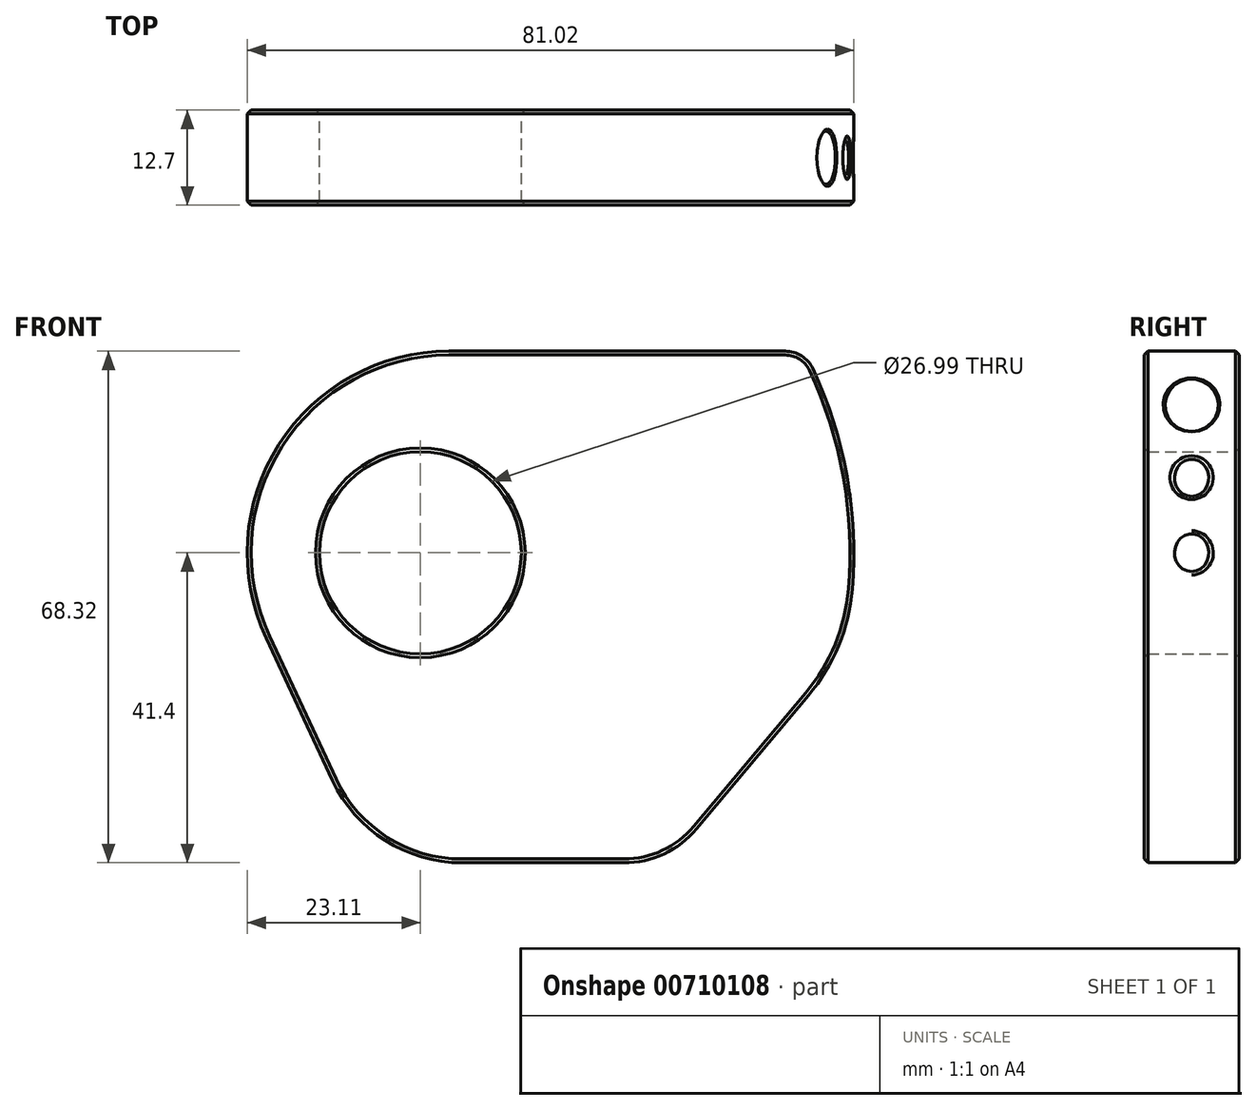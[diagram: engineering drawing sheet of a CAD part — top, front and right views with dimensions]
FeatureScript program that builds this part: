
annotation { "Feature Type Name" : "Feature", "Feature Type Description" : "" }
export const myFeature = defineFeature(function(context is Context, id is Id, definition is map)
    precondition{}
    {
        {
            assignVariable(context, id + "F0", {"name" : "DetentDepth", "anyValue" : .25});
        }
        {
            var Q0;
            Q0=qCreatedBy(makeId("Front.planeOp"),FACE);
            var sketch = newSketch(context, id + "F1", { "sketchPlane" : qUnion([Q0])});
            skCircle(sketch, "E0", {"center": v(0, 0) * mm, "radius": 13.5 * mm});
            skArc(sketch, "E1", {"start": v(57.7, -4.85) * mm, "mid": v(57, 10.21) * mm, "end": v(52.43, 24.59) * mm});
            skLineSegment(sketch, "E2", {"start": v(-46.44, 0) * mm, "end": v(76.51, 0) * mm, "construction": true});
            skLineSegment(sketch, "E3", {"start": v(0, 21.7) * mm, "end": v(0, -21.15) * mm, "construction": true});
            skArc(sketch, "E4", {"start": v(3.8, 26.92) * mm, "mid": v(-18.9, 14.47) * mm, "end": v(-20.6, -11.38) * mm});
            skLineSegment(sketch, "E5", {"start": v(3.81, 26.92) * mm, "end": v(48.75, 26.92) * mm});
            skLineSegment(sketch, "E6", {"start": v(-20.6, -11.38) * mm, "end": v(-11.72, -30.4) * mm});
            skArc(sketch, "E7", {"start": v(-11.72, -30.4) * mm, "mid": v(-4.7, -38.42) * mm, "end": v(5.54, -41.4) * mm});
            skArc(sketch, "E8", {"start": v(27.18, -41.4) * mm, "mid": v(32.55, -40.21) * mm, "end": v(36.9, -36.87) * mm});
            skArc(sketch, "E9", {"start": v(51.86, -19.05) * mm, "mid": v(55.88, -12.4) * mm, "end": v(57.7, -4.85) * mm});
            skLineSegment(sketch, "E10", {"start": v(36.9, -36.87) * mm, "end": v(51.86, -19.05) * mm});
            skLineSegment(sketch, "E11.trimOffspring", {"start": v(67.84, 0) * mm, "end": v(67.94, 0.12) * mm});
            skLineSegment(sketch, "E12.trimOffspring", {"start": v(5.54, -41.4) * mm, "end": v(27.18, -41.4) * mm});
            skArc(sketch, "E13.filletArc", {"start": v(52.43, 24.59) * mm, "mid": v(50.93, 26.29) * mm, "end": v(48.75, 26.92) * mm});
            skLineSegment(sketch, "E14", {"start": v(0, 0) * mm, "end": v(63.04, 22.95) * mm, "construction": true});
            skPoint(sketch, "E15", {"position": v(-23.11, 0) * mm});
            skPoint(sketch, "E16", {"position": v(57.91, 0) * mm});
            skLineSegment(sketch, "E17", {"start": v(-23.11, 0) * mm, "end": v(-23.11, -29.25) * mm, "construction": true});
            skLineSegment(sketch, "E18", {"start": v(27.18, -41.4) * mm, "end": v(50.41, -41.4) * mm, "construction": true});
            skLineSegment(sketch, "E19", {"start": v(0, 0) * mm, "end": v(75.03, 13.23) * mm, "construction": true});
            skPoint(sketch, "E20", {"position": v(54.42, 19.8) * mm});
            skPoint(sketch, "E21", {"position": v(57.03, 10.06) * mm});
            skLineSegment(sketch, "E22", {"start": v(52.43, 25.26) * mm, "end": v(57.13, 12.36) * mm, "construction": true});
            skLineSegment(sketch, "E23", {"start": v(55.51, 18.66) * mm, "end": v(58.4, 2.31) * mm, "construction": true});
            skLineSegment(sketch, "E24", {"start": v(57.91, 6.7) * mm, "end": v(57.91, -7.59) * mm, "construction": true});
            skText(sketch, "E25", { "text": "Design by Paula.\nSee Practical Machinist post at\n<http://www.practicalmachinist.com/vb/south-bend-lathes/10k-leadscrew-reverse-lever-installed-9-abc-129098/#post589457>\nfor original drawing.", "fontName": "OpenSans-Regular.ttf"});
            const initialGuessF1  = {"E25": [-0.45662, -0.18975, 1, 0, 0.0356]};
            skSetInitialGuess(sketch, initialGuessF1);
            skSolve(sketch);
        }
        {
            var Q0;
            Q0=makeQuery(id+"F1.imprint","IMPRINT",FACE,{"disambiguationData":[TD([[makeQuery(id+"F1.imprint","IMPRINT",EDGE,{"derivedFrom":sQuery(id+"F1.wireOp",EDGE,"E0")}),-1.0]])]});
            extrude(context, id + "F2", {"entities" : qUnion([Q0]), "depth" : 12.7 * mm, "offsetDistance" : 25.4 * mm});
        }
        {
            var Q0;
            Q0=sQuery(id+"F1.wireOp",EDGE,"E22");
            cPlane(context, id + "F3", {"entities" : qUnion([Q0]), "cplaneType" : CPlaneType.LINE_ANGLE, "offset" : 25.4 * mm, "angle" : 0 * degree, "width" : 152.4 * mm, "height" : 152.4 * mm});
        }
        {
            var Q0;
            Q0=sQuery(id+"F1.wireOp",EDGE,"E23");
            cPlane(context, id + "F4", {"entities" : qUnion([Q0]), "cplaneType" : CPlaneType.LINE_ANGLE, "offset" : 25.4 * mm, "angle" : 0 * degree, "width" : 152.4 * mm, "height" : 152.4 * mm});
        }
        {
            var Q0;
            Q0=sQuery(id+"F1.wireOp",EDGE,"E24");
            cPlane(context, id + "F5", {"entities" : qUnion([Q0]), "cplaneType" : CPlaneType.LINE_ANGLE, "offset" : 25.4 * mm, "angle" : 0 * degree, "width" : 152.4 * mm, "height" : 152.4 * mm});
        }
        {
            var Q0;
            Q0=qCreatedBy(id+"F3.planeOp",FACE);
            var sketch = newSketch(context, id + "F6", { "sketchPlane" : qUnion([Q0])});
            skPoint(sketch, "E26.0", {"position": v(12.7, 0) * mm});
            skLineSegment(sketch, "E27", {"start": v(12.7, 0) * mm, "end": v(0, 0) * mm, "construction": true});
            skLineSegment(sketch, "E28", {"start": v(6.35, 2.88) * mm, "end": v(6.35, -2.76) * mm, "construction": true});
            skPoint(sketch, "E28.startSnap0", {"position": v(6.35, 0) * mm});
            skCircle(sketch, "E29", {"center": v(6.35, 0) * mm, "radius": 3.17 * mm});
            skSolve(sketch);
        }
        {
            var Q0;
            Q0=makeQuery(id+"F6.imprint","IMPRINT",FACE,{"disambiguationData":[TD([[makeQuery(id+"F6.imprint","IMPRINT",EDGE,{"derivedFrom":sQuery(id+"F6.wireOp",EDGE,"E29")}),1.0]])]});
            extrude(context, id + "F7", {"entities" : qUnion([Q0]), "operationType" : NewBodyOperationType.REMOVE, "flatOperationType" : FlatOperationType.REMOVE, "depth" : (getVariable(context, 'DetentDepth')) * mm, "offsetDistance" : 25.4 * mm, "domain" : OperationDomain.MODEL});
        }
        {
            var Q0;
            Q0=qCreatedBy(id+"F4.planeOp",FACE);
            var sketch = newSketch(context, id + "F8", { "sketchPlane" : qUnion([Q0])});
            skPoint(sketch, "E30.startSnap0", {"position": v(6.28, 4.01) * mm});
            skPoint(sketch, "E31.0", {"position": v(12.7, 0) * mm});
            skLineSegment(sketch, "E32", {"start": v(12.7, 0) * mm, "end": v(0, 0) * mm, "construction": true});
            skLineSegment(sketch, "E33", {"start": v(6.35, 4.84) * mm, "end": v(6.35, -3.95) * mm, "construction": true});
            skPoint(sketch, "E33.startSnap0", {"position": v(6.35, 0) * mm});
            skCircle(sketch, "E34", {"center": v(6.35, 0) * mm, "radius": 3.17 * mm});
            skSolve(sketch);
        }
        {
            var Q0;
            Q0=makeQuery(id+"F8.imprint","IMPRINT",FACE,{"disambiguationData":[TD([[makeQuery(id+"F8.imprint","IMPRINT",EDGE,{"derivedFrom":sQuery(id+"F8.wireOp",EDGE,"E34")}),1.0]])]});
            extrude(context, id + "F9", {"entities" : qUnion([Q0]), "operationType" : NewBodyOperationType.REMOVE, "depth" : (getVariable(context, 'DetentDepth')) * mm, "offsetDistance" : 25.4 * mm});
        }
        {
            var Q0;
            Q0=qCreatedBy(id+"F5.planeOp",FACE);
            var sketch = newSketch(context, id + "F10", { "sketchPlane" : qUnion([Q0])});
            skPoint(sketch, "E35.0", {"position": v(12.7, 0) * mm});
            skLineSegment(sketch, "E36", {"start": v(12.7, 0) * mm, "end": v(0, 0) * mm, "construction": true});
            skLineSegment(sketch, "E37", {"start": v(6.35, 0) * mm, "end": v(6.35, 5.02) * mm, "construction": true});
            skLineSegment(sketch, "E38", {"start": v(6.35, 5.02) * mm, "end": v(6.35, -4.2) * mm, "construction": true});
            skCircle(sketch, "E39", {"center": v(6.35, 0) * mm, "radius": 3.18 * mm});
            skSolve(sketch);
        }
        {
            var Q0;
            Q0=makeQuery(id+"F10.imprint","IMPRINT",FACE,{"disambiguationData":[TD([[makeQuery(id+"F10.imprint","IMPRINT",EDGE,{"derivedFrom":sQuery(id+"F10.wireOp",EDGE,"E39")}),1.0]])]});
            extrude(context, id + "F11", {"entities" : qUnion([Q0]), "operationType" : NewBodyOperationType.REMOVE, "depth" : (getVariable(context, 'DetentDepth')) * mm, "offsetDistance" : 25.4 * mm});
        }
        {
            var Q0;
            Q0=makeQuery(id+"F7.boolean.opBoolean","INTERSECT",EDGE,{"derivedFrom":[makeQuery(id+"F2.opExtrude","SWEPT_FACE",FACE,{"disambiguationData":[OSD([sQuery(id+"F1.wireOp",EDGE,"E1")])]}),makeQuery(id+"F7.opExtrude","SWEPT_FACE",FACE,{"disambiguationData":[OSD([sQuery(id+"F6.wireOp",EDGE,"E29")])]})]});
            var Q1;
            Q1=makeQuery(id+"F9.boolean.opBoolean","INTERSECT",EDGE,{"derivedFrom":[makeQuery(id+"F2.opExtrude","SWEPT_FACE",FACE,{"disambiguationData":[OSD([sQuery(id+"F1.wireOp",EDGE,"E1")])]}),makeQuery(id+"F9.opExtrude","SWEPT_FACE",FACE,{"disambiguationData":[OSD([sQuery(id+"F8.wireOp",EDGE,"E34")])]})]});
            var Q2;
            Q2=makeQuery(id+"F11.boolean.opBoolean","INTERSECT",EDGE,{"derivedFrom":[makeQuery(id+"F2.opExtrude","SWEPT_FACE",FACE,{"disambiguationData":[OSD([sQuery(id+"F1.wireOp",EDGE,"E1")])]}),makeQuery(id+"F11.opExtrude","SWEPT_FACE",FACE,{"disambiguationData":[OSD([sQuery(id+"F10.wireOp",EDGE,"E39")])]})]});
            chamfer(context, id + "F12", {"entities" : qUnion([Q0, Q1, Q2]), "width" : 0.64 * mm, "tangentPropagation" : true});
        }
        {
            var Q0;
            Q0=makeQuery(id+"F2.opExtrude","CAP_FACE",FACE,{"disambiguationData":[OSD([sQuery(id+"F1.wireOp",EDGE,"E0"),sQuery(id+"F1.wireOp",EDGE,"E1"),sQuery(id+"F1.wireOp",EDGE,"E4"),sQuery(id+"F1.wireOp",EDGE,"E5"),sQuery(id+"F1.wireOp",EDGE,"E6"),sQuery(id+"F1.wireOp",EDGE,"E7"),sQuery(id+"F1.wireOp",EDGE,"E8"),sQuery(id+"F1.wireOp",EDGE,"E9"),sQuery(id+"F1.wireOp",EDGE,"E10"),sQuery(id+"F1.wireOp",EDGE,"E12.trimOffspring"),sQuery(id+"F1.wireOp",EDGE,"E13.filletArc")])],"isStart":false});
            var Q1;
            Q1=makeQuery(id+"F2.opExtrude","CAP_FACE",FACE,{"disambiguationData":[OSD([sQuery(id+"F1.wireOp",EDGE,"E0"),sQuery(id+"F1.wireOp",EDGE,"E1"),sQuery(id+"F1.wireOp",EDGE,"E4"),sQuery(id+"F1.wireOp",EDGE,"E5"),sQuery(id+"F1.wireOp",EDGE,"E6"),sQuery(id+"F1.wireOp",EDGE,"E7"),sQuery(id+"F1.wireOp",EDGE,"E8"),sQuery(id+"F1.wireOp",EDGE,"E9"),sQuery(id+"F1.wireOp",EDGE,"E10"),sQuery(id+"F1.wireOp",EDGE,"E12.trimOffspring"),sQuery(id+"F1.wireOp",EDGE,"E13.filletArc")])],"isStart":true});
            chamfer(context, id + "F13", {"entities" : qUnion([Q0, Q1]), "width" : 0.5 * mm, "tangentPropagation" : true});
        }
        {
            var Q0;
            Q0=makeQuery(id+"F7.boolean.opBoolean","COPY",EDGE,{"derivedFrom":makeQuery(id+"F7.opExtrude","CAP_EDGE",EDGE,{"disambiguationData":[OSD([sQuery(id+"F6.wireOp",EDGE,"E29")])],"isStart":false})});
            var Q1;
            Q1=makeQuery(id+"F9.boolean.opBoolean","COPY",FACE,{"derivedFrom":makeQuery(id+"F9.opExtrude","CAP_FACE",FACE,{"disambiguationData":[OSD([sQuery(id+"F8.wireOp",EDGE,"E34")])],"isStart":false})});
            var Q2;
            Q2=makeQuery(id+"F11.boolean.opBoolean","COPY",FACE,{"derivedFrom":makeQuery(id+"F11.opExtrude","CAP_FACE",FACE,{"disambiguationData":[OSD([sQuery(id+"F10.wireOp",EDGE,"E39")])],"isStart":false})});
            chamfer(context, id + "F14", {"entities" : qUnion([Q0, Q1, Q2]), "width" : 3.05 * mm, "tangentPropagation" : true});
        }
    });
